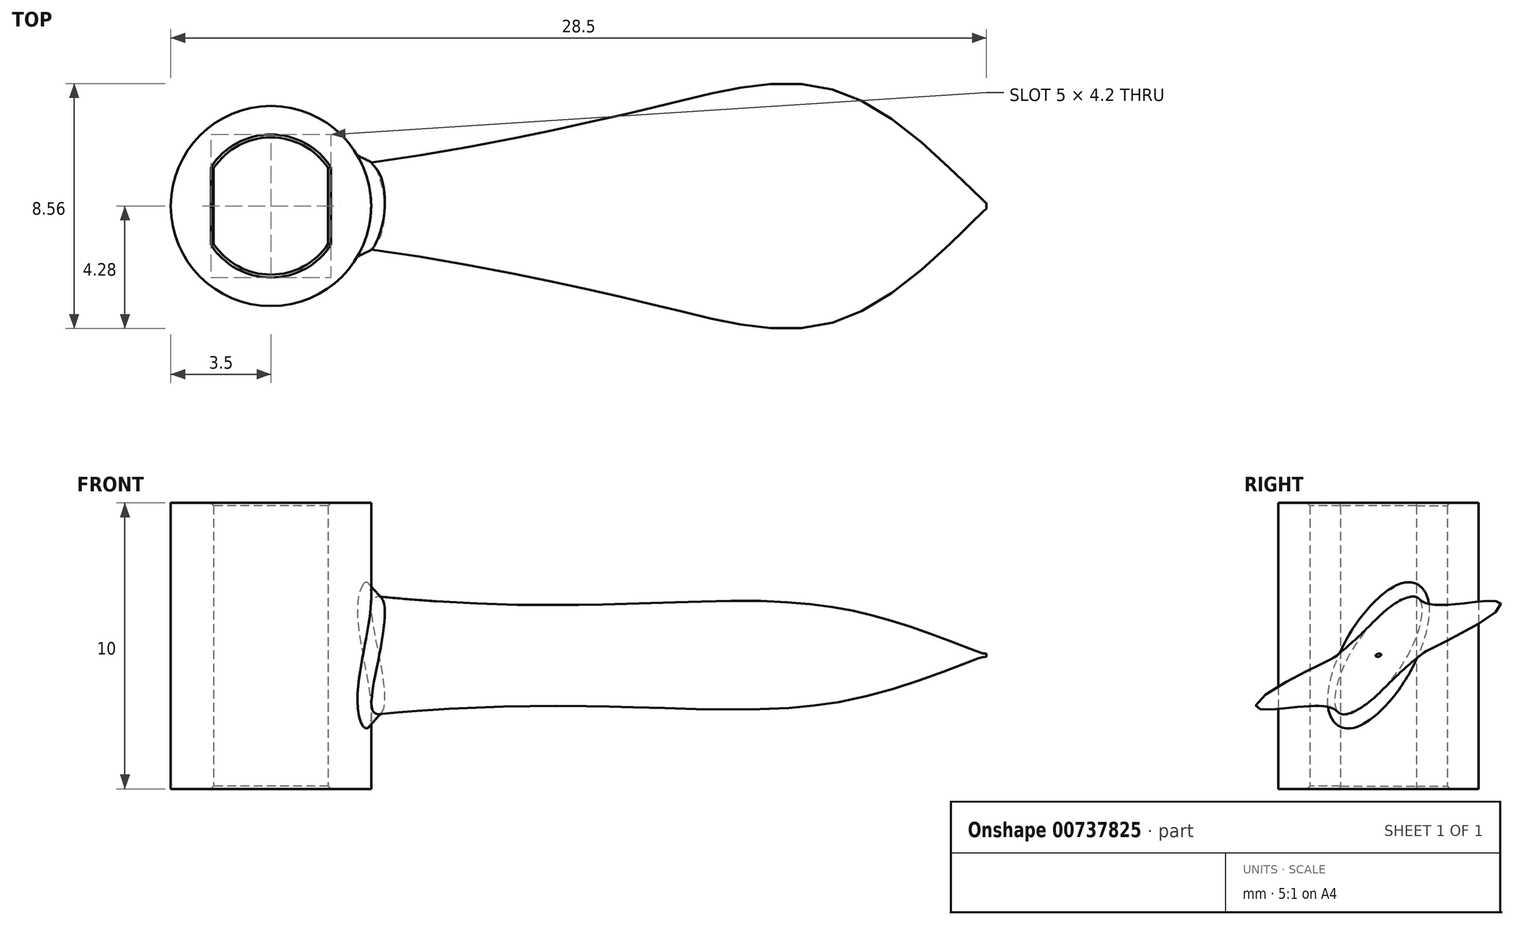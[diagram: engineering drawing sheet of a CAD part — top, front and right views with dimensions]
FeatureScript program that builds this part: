
annotation { "Feature Type Name" : "Feature", "Feature Type Description" : "" }
export const myFeature = defineFeature(function(context is Context, id is Id, definition is map)
    precondition{}
    {
        {
            var Q0;
            Q0=qCreatedBy(makeId("Top.planeOp"),FACE);
            var sketch = newSketch(context, id + "F0", { "sketchPlane" : qUnion([Q0])});
            skCircle(sketch, "E0", {"center": v(0, 0) * mm, "radius": 2.4 * mm});
            skLineSegment(sketch, "E1", {"start": v(-2, 1.33) * mm, "end": v(2, 1.33) * mm});
            skLineSegment(sketch, "E2", {"start": v(-2, -1.33) * mm, "end": v(2, -1.33) * mm});
            skLineSegment(sketch, "E3", {"start": v(-2, 1.33) * mm, "end": v(-2, -1.33) * mm});
            skLineSegment(sketch, "E4", {"start": v(2, 1.33) * mm, "end": v(2, -1.33) * mm});
            skCircle(sketch, "E5", {"center": v(0, 0) * mm, "radius": 3.5 * mm});
            skSolve(sketch);
        }
        {
            var Q0;
            {var subQ0=sQuery(id+"F0.wireOp",EDGE,"E3");Q0=makeQuery(id+"F0.imprint","IMPRINT",FACE,{"disambiguationData":[TD([[makeQuery(id+"F0.imprint","IMPRINT",EDGE,{"derivedFrom":subQ0}),-1.0]])]});}
            var Q1;
            {var subQ0=sQuery(id+"F0.wireOp",EDGE,"E4");Q1=makeQuery(id+"F0.imprint","IMPRINT",FACE,{"disambiguationData":[TD([[makeQuery(id+"F0.imprint","IMPRINT",EDGE,{"derivedFrom":subQ0}),1.0]])]});}
            var Q2;
            Q2=makeQuery(id+"F0.imprint","IMPRINT",FACE,{"disambiguationData":[TD([[makeQuery(id+"F0.imprint","IMPRINT",EDGE,{"derivedFrom":sQuery(id+"F0.wireOp",EDGE,"E5")}),1.0]])]});
            extrude(context, id + "F1", {"entities" : qUnion([Q0, Q1, Q2]), "flatOperationType" : FlatOperationType.REMOVE, "depth" : 10 * mm, "offsetDistance" : 25 * mm, "domain" : OperationDomain.MODEL});
        }
        {
            var Q0;
            Q0=makeQuery(id+"F1.opExtrude","CAP_EDGE",EDGE,{"disambiguationData":[OSD([sQuery(id+"F0.wireOp",EDGE,"E3")])],"isStart":true});
            var Q1;
            {var subQ0=sQuery(id+"F0.wireOp",EDGE,"E1");var subQ1=sQuery(id+"F0.wireOp",EDGE,"E0");Q1=makeQuery(id+"F1.opExtrude","CAP_EDGE",EDGE,{"disambiguationData":[OSD([subQ1]),TDD([makeQuery(id+"F0.imprint","IMPRINT",EDGE,{"disambiguationData":[TD([[makeQuery(id+"F0.imprint","INTERSECT",VERTEX,{"derivedFrom":[subQ1,subQ0,sQuery(id+"F0.wireOp",EDGE,"E3")]}),1.0]])],"derivedFrom":subQ1})])],"isStart":true});}
            var Q2;
            Q2=makeQuery(id+"F1.opExtrude","CAP_EDGE",EDGE,{"disambiguationData":[OSD([sQuery(id+"F0.wireOp",EDGE,"E4")])],"isStart":true});
            var Q3;
            {var subQ0=sQuery(id+"F0.wireOp",EDGE,"E2");var subQ1=sQuery(id+"F0.wireOp",EDGE,"E0");Q3=makeQuery(id+"F1.opExtrude","CAP_EDGE",EDGE,{"disambiguationData":[OSD([subQ1]),TDD([makeQuery(id+"F0.imprint","IMPRINT",EDGE,{"disambiguationData":[TD([[makeQuery(id+"F0.imprint","INTERSECT",VERTEX,{"derivedFrom":[subQ1,subQ0,sQuery(id+"F0.wireOp",EDGE,"E3")]}),-1.0]])],"derivedFrom":subQ1})])],"isStart":true});}
            var Q4;
            {var subQ0=sQuery(id+"F0.wireOp",EDGE,"E2");var subQ1=sQuery(id+"F0.wireOp",EDGE,"E0");Q4=makeQuery(id+"F1.opExtrude","CAP_EDGE",EDGE,{"disambiguationData":[OSD([subQ1]),TDD([makeQuery(id+"F0.imprint","IMPRINT",EDGE,{"disambiguationData":[TD([[makeQuery(id+"F0.imprint","INTERSECT",VERTEX,{"derivedFrom":[subQ1,subQ0,sQuery(id+"F0.wireOp",EDGE,"E3")]}),-1.0]])],"derivedFrom":subQ1})])],"isStart":false});}
            var Q5;
            Q5=makeQuery(id+"F1.opExtrude","CAP_EDGE",EDGE,{"disambiguationData":[OSD([sQuery(id+"F0.wireOp",EDGE,"E4")])],"isStart":false});
            var Q6;
            {var subQ0=sQuery(id+"F0.wireOp",EDGE,"E1");var subQ1=sQuery(id+"F0.wireOp",EDGE,"E0");Q6=makeQuery(id+"F1.opExtrude","CAP_EDGE",EDGE,{"disambiguationData":[OSD([subQ1]),TDD([makeQuery(id+"F0.imprint","IMPRINT",EDGE,{"disambiguationData":[TD([[makeQuery(id+"F0.imprint","INTERSECT",VERTEX,{"derivedFrom":[subQ1,subQ0,sQuery(id+"F0.wireOp",EDGE,"E3")]}),1.0]])],"derivedFrom":subQ1})])],"isStart":false});}
            var Q7;
            Q7=makeQuery(id+"F1.opExtrude","CAP_EDGE",EDGE,{"disambiguationData":[OSD([sQuery(id+"F0.wireOp",EDGE,"E3")])],"isStart":false});
            chamfer(context, id + "F2", {"entities" : qUnion([Q0, Q1, Q2, Q3, Q4, Q5, Q6, Q7]), "width" : 0.1 * mm, "tangentPropagation" : true});
        }
        {
            var Q0;
            Q0=qCreatedBy(makeId("Right.planeOp"),FACE);
            cPlane(context, id + "F3", {"entities" : qUnion([Q0]), "cplaneType" : CPlaneType.OFFSET, "offset" : 2.5 * mm, "width" : 150 * mm, "height" : 150 * mm});
        }
        {
            var Q0;
            Q0=qCreatedBy(makeId("Right.planeOp"),FACE);
            cPlane(context, id + "F4", {"entities" : qUnion([Q0]), "cplaneType" : CPlaneType.OFFSET, "offset" : 6 * mm, "width" : 150 * mm, "height" : 150 * mm});
        }
        {
            var Q0;
            Q0=qCreatedBy(makeId("Right.planeOp"),FACE);
            cPlane(context, id + "F5", {"entities" : qUnion([Q0]), "cplaneType" : CPlaneType.OFFSET, "offset" : 14 * mm, "width" : 150 * mm, "height" : 150 * mm});
        }
        {
            var Q0;
            Q0=qCreatedBy(makeId("Right.planeOp"),FACE);
            cPlane(context, id + "F6", {"entities" : qUnion([Q0]), "cplaneType" : CPlaneType.OFFSET, "offset" : 20 * mm, "width" : 150 * mm, "height" : 150 * mm});
        }
        {
            var Q0;
            Q0=qCreatedBy(makeId("Right.planeOp"),FACE);
            cPlane(context, id + "F7", {"entities" : qUnion([Q0]), "cplaneType" : CPlaneType.OFFSET, "offset" : 25 * mm, "width" : 150 * mm, "height" : 150 * mm});
        }
        {
            var Q0;
            Q0=qCreatedBy(id+"F3.planeOp",FACE);
            var sketch = newSketch(context, id + "F8", { "sketchPlane" : qUnion([Q0])});
            skEllipse(sketch, "E6", {"center": v(0, 4.67) * mm, "majorRadius": 2.5 * mm, "minorRadius": 0.75 * mm, "majorAxis": v(0.5, 0.86)});
            skSolve(sketch);
        }
        {
            var Q0;
            Q0=qCreatedBy(id+"F5.planeOp",FACE);
            var sketch = newSketch(context, id + "F9", { "sketchPlane" : qUnion([Q0])});
            skEllipse(sketch, "E7", {"center": v(0, 4.67) * mm, "majorRadius": 4 * mm, "minorRadius": 0.65 * mm, "majorAxis": v(0.9, 0.44)});
            skSolve(sketch);
        }
        {
            var Q0;
            Q0=qCreatedBy(id+"F6.planeOp",FACE);
            var sketch = newSketch(context, id + "F10", { "sketchPlane" : qUnion([Q0])});
            skEllipse(sketch, "E8", {"center": v(0, 4.68) * mm, "majorRadius": 4.25 * mm, "minorRadius": 0.45 * mm, "majorAxis": v(0.93, 0.37)});
            skSolve(sketch);
        }
        {
            var Q0;
            Q0=qCreatedBy(id+"F7.planeOp",FACE);
            var sketch = newSketch(context, id + "F11", { "sketchPlane" : qUnion([Q0])});
            skEllipse(sketch, "E9", {"center": v(0, 4.67) * mm, "majorRadius": 0.1 * mm, "minorRadius": 0.05 * mm, "majorAxis": v(0.97, 0.24)});
            skSolve(sketch);
        }
        {
            var Q1;
            Q1 = qSketchRegion(id + "F8", true);
            var Q2;
            Q2 = qSketchRegion(id + "F9", true);
            var Q3;
            Q3 = qSketchRegion(id + "F10", true);
            var Q4;
            Q4 = qSketchRegion(id + "F11", true);
            loft(context, id + "F12", {"operationType" : NewBodyOperationType.ADD, "sheetProfilesArray" : [{ "sheetProfileEntities" : qUnion([Q1]) }, { "sheetProfileEntities" : qUnion([Q2]) }, { "sheetProfileEntities" : qUnion([Q3]) }, { "sheetProfileEntities" : qUnion([Q4]) }], "trimGuidesByProfiles" : true});
        }
        {
            var Q0;
            Q0=makeQuery(id+"F12.boolean.opBoolean","INTERSECT",EDGE,{"derivedFrom":[makeQuery(id+"F1.opExtrude","SWEPT_FACE",FACE,{"disambiguationData":[OSD([sQuery(id+"F0.wireOp",EDGE,"E5")])]}),makeQuery(id+"F12.opLoft","SWEPT_FACE",FACE,{"disambiguationData":[OSD([sQuery(id+"F8.wireOp",EDGE,"E6"),sQuery(id+"F9.wireOp",EDGE,"E7")])]})]});
            var Q1;
            Q1=makeQuery(id+"Fe8MJzp70RLVtrY_1.1.F12.boolean.opBoolean","INTERSECT",EDGE,{"derivedFrom":[makeQuery(id+"F1.opExtrude","SWEPT_FACE",FACE,{"disambiguationData":[OSD([sQuery(id+"F0.wireOp",EDGE,"E5")])]}),makeQuery(id+"Fe8MJzp70RLVtrY_1.1.F12.opLoft","SWEPT_FACE",FACE,{"disambiguationData":[OSD([sQuery(id+"F8.wireOp",EDGE,"E6"),sQuery(id+"F9.wireOp",EDGE,"E7")])]})]});
            var Q2;
            Q2=makeQuery(id+"Fe8MJzp70RLVtrY_1.2.F12.boolean.opBoolean","INTERSECT",EDGE,{"derivedFrom":[makeQuery(id+"F1.opExtrude","SWEPT_FACE",FACE,{"disambiguationData":[OSD([sQuery(id+"F0.wireOp",EDGE,"E5")])]}),makeQuery(id+"Fe8MJzp70RLVtrY_1.2.F12.opLoft","SWEPT_FACE",FACE,{"disambiguationData":[OSD([sQuery(id+"F8.wireOp",EDGE,"E6"),sQuery(id+"F9.wireOp",EDGE,"E7")])]})]});
            chamfer(context, id + "F13", {"entities" : qUnion([Q0, Q1, Q2]), "width" : 0.5 * mm, "tangentPropagation" : true});
        }
    });
